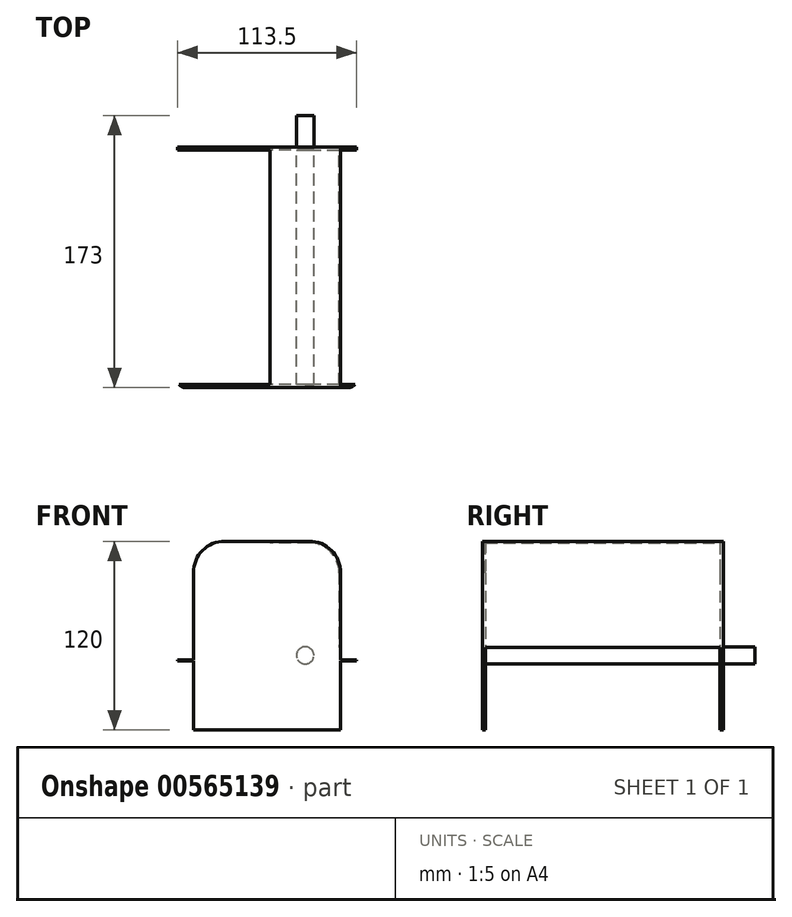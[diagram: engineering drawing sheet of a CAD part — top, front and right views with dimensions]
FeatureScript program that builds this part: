
annotation { "Feature Type Name" : "Feature", "Feature Type Description" : "" }
export const myFeature = defineFeature(function(context is Context, id is Id, definition is map)
    precondition{}
    {
        {
            var Q0;
            Q0=qCreatedBy(makeId("Front.planeOp"),FACE);
            var sketch = newSketch(context, id + "F0", { "sketchPlane" : qUnion([Q0])});
            skLineSegment(sketch, "E0.bottom", {"start": v(46.75, 60) * mm, "end": v(-46.75, 60) * mm});
            skLineSegment(sketch, "E0.top", {"start": v(46.75, -60) * mm, "end": v(-46.75, -60) * mm});
            skLineSegment(sketch, "E0.left", {"start": v(46.75, 60) * mm, "end": v(46.75, -60) * mm});
            skLineSegment(sketch, "E0.right", {"start": v(-46.75, 60) * mm, "end": v(-46.75, -60) * mm});
            skPoint(sketch, "E0.middle", {"position": v(0, 0) * mm});
            skCircle(sketch, "E1", {"center": v(-26.75, 40) * mm, "radius": 20 * mm});
            skPoint(sketch, "E1.first.point", {"position": v(-26.75, 60) * mm});
            skPoint(sketch, "E1.second.point", {"position": v(-46.75, 40) * mm});
            skPoint(sketch, "E1.third.point", {"position": v(-9.2, 30.42) * mm});
            skCircle(sketch, "E2", {"center": v(26.75, 40) * mm, "radius": 20 * mm});
            skPoint(sketch, "E2.first.point", {"position": v(26.75, 60) * mm});
            skPoint(sketch, "E2.second.point", {"position": v(46.75, 40) * mm});
            skPoint(sketch, "E2.third.point", {"position": v(10.34, 28.57) * mm});
            skSolve(sketch);
        }
        {
            var Q0;
            {var subQ1=sQuery(id+"F0.wireOp",EDGE,"E0.top");Q0=makeQuery(id+"F0.imprint","IMPRINT",FACE,{"disambiguationData":[TD([[makeQuery(id+"F0.imprint","IMPRINT",EDGE,{"derivedFrom":subQ1}),-1.0]])]});}
            var Q1;
            {var subQ0=sQuery(id+"F0.wireOp",EDGE,"E2");var subQ1=makeQuery(id+"F0.imprint","INTERSECT",VERTEX,{"derivedFrom":[sQuery(id+"F0.wireOp",EDGE,"E0.bottom"),subQ0]});Q1=makeQuery(id+"F0.imprint","IMPRINT",FACE,{"disambiguationData":[TD([[makeQuery(id+"F0.imprint","IMPRINT",EDGE,{"disambiguationData":[TD([[subQ1,1.0]])],"derivedFrom":subQ0}),1.0]])]});}
            var Q2;
            {var subQ0=sQuery(id+"F0.wireOp",EDGE,"E1");var subQ1=makeQuery(id+"F0.imprint","INTERSECT",VERTEX,{"derivedFrom":[sQuery(id+"F0.wireOp",EDGE,"E0.bottom"),subQ0]});Q2=makeQuery(id+"F0.imprint","IMPRINT",FACE,{"disambiguationData":[TD([[makeQuery(id+"F0.imprint","IMPRINT",EDGE,{"disambiguationData":[TD([[subQ1,-1.0]])],"derivedFrom":subQ0}),1.0]])]});}
            extrude(context, id + "F1", {"entities" : qUnion([Q0, Q1, Q2]), "endBound" : BoundingType.SYMMETRIC, "depth" : 153 * mm, "offsetDistance" : 25 * mm});
        }
        {
            var Q0;
            Q0=makeQuery(id+"F1.opExtrude","CAP_FACE",FACE,{"disambiguationData":[OSD([sQuery(id+"F0.wireOp",EDGE,"E0.bottom"),sQuery(id+"F0.wireOp",EDGE,"E0.top"),sQuery(id+"F0.wireOp",EDGE,"E0.left"),sQuery(id+"F0.wireOp",EDGE,"E0.right"),sQuery(id+"F0.wireOp",EDGE,"E1"),sQuery(id+"F0.wireOp",EDGE,"E2")])],"isStart":false});
            var sketch = newSketch(context, id + "F2", { "sketchPlane" : qUnion([Q0])});
            skLineSegment(sketch, "E3.bottom", {"start": v(56.75, -15.5) * mm, "end": v(-56.75, -15.5) * mm});
            skLineSegment(sketch, "E3.top", {"start": v(56.75, -16) * mm, "end": v(-56.75, -16) * mm});
            skLineSegment(sketch, "E3.left", {"start": v(56.75, -15.5) * mm, "end": v(56.75, -16) * mm});
            skLineSegment(sketch, "E3.right", {"start": v(-56.75, -15.5) * mm, "end": v(-56.75, -16) * mm});
            skSolve(sketch);
        }
        {
            var Q0;
            Q0 = qSketchRegion(id + "F2", true);
            var Q1;
            Q1=makeQuery(id+"F1.opExtrude","CAP_FACE",FACE,{"disambiguationData":[OSD([sQuery(id+"F0.wireOp",EDGE,"E0.bottom"),sQuery(id+"F0.wireOp",EDGE,"E0.top"),sQuery(id+"F0.wireOp",EDGE,"E0.left"),sQuery(id+"F0.wireOp",EDGE,"E0.right"),sQuery(id+"F0.wireOp",EDGE,"E1"),sQuery(id+"F0.wireOp",EDGE,"E2")])],"isStart":true});
            extrude(context, id + "F3", {"entities" : qUnion([Q0]), "operationType" : NewBodyOperationType.ADD, "endBound" : BoundingType.UP_TO_SURFACE, "oppositeDirection" : true, "depth" : 25 * mm, "endBoundEntityFace" : qUnion([Q1]), "offsetDistance" : 25 * mm});
        }
        {
            var Q0;
            Q0=makeQuery(id+"F3.opExtrude","TWEAK_EDGE",EDGE,{"derivedFrom":[makeQuery(id+"F1.opExtrude","CAP_FACE",FACE,{"disambiguationData":[OSD([sQuery(id+"F0.wireOp",EDGE,"E0.bottom"),sQuery(id+"F0.wireOp",EDGE,"E0.top"),sQuery(id+"F0.wireOp",EDGE,"E0.left"),sQuery(id+"F0.wireOp",EDGE,"E0.right"),sQuery(id+"F0.wireOp",EDGE,"E1"),sQuery(id+"F0.wireOp",EDGE,"E2")])],"isStart":true}),makeQuery(id+"F2.imprint","IMPRINT",EDGE,{"derivedFrom":sQuery(id+"F2.wireOp",EDGE,"E3.left")})]});
            var Q1;
            Q1=makeQuery(id+"F3.opExtrude","TWEAK_EDGE",EDGE,{"derivedFrom":[makeQuery(id+"F1.opExtrude","CAP_FACE",FACE,{"disambiguationData":[OSD([sQuery(id+"F0.wireOp",EDGE,"E0.bottom"),sQuery(id+"F0.wireOp",EDGE,"E0.top"),sQuery(id+"F0.wireOp",EDGE,"E0.left"),sQuery(id+"F0.wireOp",EDGE,"E0.right"),sQuery(id+"F0.wireOp",EDGE,"E1"),sQuery(id+"F0.wireOp",EDGE,"E2")])],"isStart":true}),makeQuery(id+"F2.imprint","IMPRINT",EDGE,{"derivedFrom":sQuery(id+"F2.wireOp",EDGE,"E3.right")})]});
            var Q2;
            Q2=makeQuery(id+"F3.opExtrude","CAP_EDGE",EDGE,{"disambiguationData":[OSD([sQuery(id+"F2.wireOp",EDGE,"E3.right")])],"isStart":true});
            var Q3;
            Q3=makeQuery(id+"F3.opExtrude","CAP_EDGE",EDGE,{"disambiguationData":[OSD([sQuery(id+"F2.wireOp",EDGE,"E3.left")])],"isStart":true});
            fillet(context, id + "F4", {"entities" : qUnion([Q0, Q1, Q2, Q3]), "radius" : 5 * mm, "tangentPropagation" : true, "allowEdgeOverflow" : false});
        }
        {
            var Q0;
            {var subQ2=sQuery(id+"F0.wireOp",EDGE,"E0.right");var subQ7=sQuery(id+"F2.wireOp",EDGE,"E3.bottom");Q0=makeQuery(id+"F3.boolean.opBoolean","SPLIT",FACE,{"disambiguationData":[TD([makeQuery(id+"F1.opExtrude","SWEPT_FACE",FACE,{"disambiguationData":[OSD([subQ2])]})])],"derivedFrom":makeQuery(id+"F3.opExtrude","SWEPT_FACE",FACE,{"disambiguationData":[OSD([subQ7])]})});}
            var sketch = newSketch(context, id + "F5", { "sketchPlane" : qUnion([Q0])});
            skLineSegment(sketch, "E4", {"start": v(-56.75, 71.5) * mm, "end": v(-46.75, 71.5) * mm, "construction": true});
            skLineSegment(sketch, "E5", {"start": v(-51.75, 71.5) * mm, "end": v(-51.75, 69.11) * mm, "construction": true});
            skLineSegment(sketch, "E6", {"start": v(-51.75, 62.95) * mm, "end": v(-51.75, 61.45) * mm});
            skArc(sketch, "E7.0.startCap", {"start": v(-53.8, 62.95) * mm, "mid": v(-51.75, 65) * mm, "end": v(-49.7, 62.95) * mm});
            skArc(sketch, "E7.0.endCap", {"start": v(-49.7, 61.45) * mm, "mid": v(-51.75, 59.4) * mm, "end": v(-53.8, 61.45) * mm});
            skLineSegment(sketch, "E7.0.left", {"start": v(-49.7, 62.95) * mm, "end": v(-49.7, 61.45) * mm});
            skLineSegment(sketch, "E7.0.right", {"start": v(-53.8, 62.95) * mm, "end": v(-53.8, 61.45) * mm});
            skLineSegment(sketch, "E8.0.1.0", {"start": v(-51.75, 11.05) * mm, "end": v(-51.75, 9.55) * mm});
            skLineSegment(sketch, "E8.0.1.1", {"start": v(-53.8, 11.05) * mm, "end": v(-53.8, 9.55) * mm});
            skArc(sketch, "E8.0.1.2", {"start": v(-49.7, 9.55) * mm, "mid": v(-51.75, 7.5) * mm, "end": v(-53.8, 9.55) * mm});
            skArc(sketch, "E8.0.1.3", {"start": v(-53.8, 11.05) * mm, "mid": v(-51.75, 13.1) * mm, "end": v(-49.7, 11.05) * mm});
            skLineSegment(sketch, "E8.0.1.4", {"start": v(-49.7, 11.05) * mm, "end": v(-49.7, 9.55) * mm});
            skLineSegment(sketch, "E8.1.0.0", {"start": v(52.25, 62.95) * mm, "end": v(52.25, 61.45) * mm});
            skLineSegment(sketch, "E8.1.0.1", {"start": v(50.2, 62.95) * mm, "end": v(50.2, 61.45) * mm});
            skArc(sketch, "E8.1.0.2", {"start": v(54.3, 61.45) * mm, "mid": v(52.25, 59.4) * mm, "end": v(50.2, 61.45) * mm});
            skArc(sketch, "E8.1.0.3", {"start": v(50.2, 62.95) * mm, "mid": v(52.25, 65) * mm, "end": v(54.3, 62.95) * mm});
            skLineSegment(sketch, "E8.1.0.4", {"start": v(54.3, 62.95) * mm, "end": v(54.3, 61.45) * mm});
            skLineSegment(sketch, "E8.1.1.0", {"start": v(52.25, 11.05) * mm, "end": v(52.25, 9.55) * mm});
            skLineSegment(sketch, "E8.1.1.1", {"start": v(50.2, 11.05) * mm, "end": v(50.2, 9.55) * mm});
            skArc(sketch, "E8.1.1.2", {"start": v(54.3, 9.55) * mm, "mid": v(52.25, 7.5) * mm, "end": v(50.2, 9.55) * mm});
            skArc(sketch, "E8.1.1.3", {"start": v(50.2, 11.05) * mm, "mid": v(52.25, 13.1) * mm, "end": v(54.3, 11.05) * mm});
            skLineSegment(sketch, "E8.1.1.4", {"start": v(54.3, 11.05) * mm, "end": v(54.3, 9.55) * mm});
            skLineSegment(sketch, "E8.direction1", {"start": v(-51.75, 61.45) * mm, "end": v(52.25, 61.45) * mm, "construction": true});
            skLineSegment(sketch, "E8.direction2", {"start": v(-51.75, 61.45) * mm, "end": v(-51.75, 9.55) * mm, "construction": true});
            skLineSegment(sketch, "E9", {"start": v(-56.75, 0) * mm, "end": v(-85.02, 0) * mm, "construction": true});
            skArc(sketch, "E10.MirrorCS", {"start": v(-49.7, -61.45) * mm, "mid": v(-51.75, -59.4) * mm, "end": v(-53.8, -61.45) * mm});
            skArc(sketch, "E11.MirrorCS", {"start": v(-53.8, -11.05) * mm, "mid": v(-51.75, -13.1) * mm, "end": v(-49.7, -11.05) * mm});
            skArc(sketch, "E12.MirrorCS", {"start": v(-49.7, -9.55) * mm, "mid": v(-51.75, -7.5) * mm, "end": v(-53.8, -9.55) * mm});
            skLineSegment(sketch, "E13.MirrorCS", {"start": v(-49.7, -11.05) * mm, "end": v(-49.7, -9.55) * mm});
            skLineSegment(sketch, "E14.MirrorCS", {"start": v(-53.8, -11.05) * mm, "end": v(-53.8, -9.55) * mm});
            skArc(sketch, "E15.MirrorCS", {"start": v(-53.8, -62.95) * mm, "mid": v(-51.75, -65) * mm, "end": v(-49.7, -62.95) * mm});
            skLineSegment(sketch, "E16.MirrorCS", {"start": v(-53.8, -62.95) * mm, "end": v(-53.8, -61.45) * mm});
            skLineSegment(sketch, "E17.MirrorCS", {"start": v(-49.7, -62.95) * mm, "end": v(-49.7, -61.45) * mm});
            skArc(sketch, "E18.MirrorCS", {"start": v(54.3, -9.55) * mm, "mid": v(52.25, -7.5) * mm, "end": v(50.2, -9.55) * mm});
            skArc(sketch, "E19.MirrorCS", {"start": v(50.2, -11.05) * mm, "mid": v(52.25, -13.1) * mm, "end": v(54.3, -11.05) * mm});
            skLineSegment(sketch, "E20.MirrorCS", {"start": v(50.2, -11.05) * mm, "end": v(50.2, -9.55) * mm});
            skLineSegment(sketch, "E21.MirrorCS", {"start": v(54.3, -11.05) * mm, "end": v(54.3, -9.55) * mm});
            skArc(sketch, "E22.MirrorCS", {"start": v(54.3, -61.45) * mm, "mid": v(52.25, -59.4) * mm, "end": v(50.2, -61.45) * mm});
            skArc(sketch, "E23.MirrorCS", {"start": v(50.2, -62.95) * mm, "mid": v(52.25, -65) * mm, "end": v(54.3, -62.95) * mm});
            skLineSegment(sketch, "E24.MirrorCS", {"start": v(50.2, -62.95) * mm, "end": v(50.2, -61.45) * mm});
            skLineSegment(sketch, "E25.MirrorCS", {"start": v(54.3, -62.95) * mm, "end": v(54.3, -61.45) * mm});
            skSolve(sketch);
        }
        {
            var Q0;
            Q0 = qSketchRegion(id + "F5", true);
            extrude(context, id + "F6", {"entities" : qUnion([Q0]), "operationType" : NewBodyOperationType.REMOVE, "endBound" : BoundingType.THROUGH_ALL, "oppositeDirection" : true, "depth" : 25 * mm, "offsetDistance" : 25 * mm});
        }
        {
            var Q0;
            {var subQ0=sQuery(id+"F0.wireOp",EDGE,"E2");var subQ1=sQuery(id+"F0.wireOp",EDGE,"E1");var subQ2=sQuery(id+"F0.wireOp",EDGE,"E0.right");var subQ3=sQuery(id+"F0.wireOp",EDGE,"E0.left");var subQ4=sQuery(id+"F0.wireOp",EDGE,"E0.top");var subQ5=sQuery(id+"F0.wireOp",EDGE,"E0.bottom");Q0=makeQuery(id+"F3.boolean.opBoolean","MERGE",FACE,{"derivedFrom":[makeQuery(id+"F1.opExtrude","CAP_FACE",FACE,{"disambiguationData":[OSD([subQ5,subQ4,subQ3,subQ2,subQ1,subQ0])],"isStart":true}),makeQuery(id+"F3.opExtrude","CAP_FACE",FACE,{"disambiguationData":[OSD([subQ5,subQ4,subQ3,subQ2,subQ1,subQ0])],"isStart":false})]});}
            var sketch = newSketch(context, id + "F7", { "sketchPlane" : qUnion([Q0])});
            skCircle(sketch, "E26", {"center": v(-24.25, -12.5) * mm, "radius": 5.5 * mm});
            skSolve(sketch);
        }
        {
            var Q0;
            Q0 = qSketchRegion(id + "F7", true);
            extrude(context, id + "F8", {"entities" : qUnion([Q0]), "operationType" : NewBodyOperationType.ADD, "depth" : 20 * mm, "offsetDistance" : 25 * mm});
        }
        {
            var Q0;
            Q0=makeQuery(id+"F1.opExtrude","SWEPT_FACE",FACE,{"disambiguationData":[OSD([sQuery(id+"F0.wireOp",EDGE,"E0.top")])]});
            var sketch = newSketch(context, id + "F9", { "sketchPlane" : qUnion([Q0])});
            skLineSegment(sketch, "E27.bottom", {"start": v(-41.25, -56.5) * mm, "end": v(41.25, -56.5) * mm});
            skLineSegment(sketch, "E27.top", {"start": v(-41.25, 56.5) * mm, "end": v(41.25, 56.5) * mm});
            skLineSegment(sketch, "E27.left", {"start": v(-41.25, -56.5) * mm, "end": v(-41.25, 56.5) * mm});
            skLineSegment(sketch, "E27.right", {"start": v(41.25, -56.5) * mm, "end": v(41.25, 56.5) * mm});
            skSolve(sketch);
        }
        {
            var Q0;
            Q0 = qSketchRegion(id + "F9", true);
            extrude(context, id + "F10", {"entities" : qUnion([Q0]), "operationType" : NewBodyOperationType.REMOVE, "oppositeDirection" : true, "depth" : 6 * mm, "offsetDistance" : 25 * mm});
        }
        {
            var Q0;
            {var subQ0=sQuery(id+"F0.wireOp",EDGE,"E2");var subQ1=sQuery(id+"F0.wireOp",EDGE,"E1");var subQ2=sQuery(id+"F0.wireOp",EDGE,"E0.right");var subQ3=sQuery(id+"F0.wireOp",EDGE,"E0.left");var subQ4=sQuery(id+"F0.wireOp",EDGE,"E0.top");var subQ5=sQuery(id+"F0.wireOp",EDGE,"E0.bottom");Q0=makeQuery(id+"F3.boolean.opBoolean","MERGE",FACE,{"derivedFrom":[makeQuery(id+"F1.opExtrude","CAP_FACE",FACE,{"disambiguationData":[OSD([subQ5,subQ4,subQ3,subQ2,subQ1,subQ0])],"isStart":true}),makeQuery(id+"F3.opExtrude","CAP_FACE",FACE,{"disambiguationData":[OSD([subQ5,subQ4,subQ3,subQ2,subQ1,subQ0])],"isStart":false})]});}
            var sketch = newSketch(context, id + "F11", { "sketchPlane" : qUnion([Q0])});
            skLineSegment(sketch, "E28.0", {"start": v(-26.75, 59) * mm, "end": v(26.75, 59) * mm});
            skArc(sketch, "E28.1", {"start": v(-45.75, 40) * mm, "mid": v(-40.19, 53.44) * mm, "end": v(-26.75, 59) * mm});
            skLineSegment(sketch, "E28.2", {"start": v(-45.75, 40) * mm, "end": v(-45.75, -15.5) * mm});
            skLineSegment(sketch, "E29.0", {"start": v(-26.75, 54) * mm, "end": v(26.75, 54) * mm});
            skArc(sketch, "E29.1", {"start": v(-40.75, 40) * mm, "mid": v(-36.65, 49.9) * mm, "end": v(-26.75, 54) * mm});
            skLineSegment(sketch, "E29.2", {"start": v(-40.75, 40) * mm, "end": v(-40.75, -15.5) * mm});
            skArc(sketch, "E30.0", {"start": v(-46.75, 40) * mm, "mid": v(-40.9, 54.14) * mm, "end": v(-26.75, 60) * mm});
            skLineSegment(sketch, "E31.0", {"start": v(-26.75, 60) * mm, "end": v(26.75, 60) * mm});
            skLineSegment(sketch, "E32.0", {"start": v(-46.75, 40) * mm, "end": v(-46.75, -15.5) * mm});
            skLineSegment(sketch, "E33", {"start": v(-46.75, -7.5) * mm, "end": v(-45.75, -7.5) * mm});
            skLineSegment(sketch, "E34", {"start": v(0, 60) * mm, "end": v(0, 49.87) * mm, "construction": true});
            skLineSegment(sketch, "E35", {"start": v(-2, 60) * mm, "end": v(-2, 59) * mm});
            skSolve(sketch);
        }
        {
            var Q0;
            {var subQ2=sQuery(id+"F11.wireOp",EDGE,"E28.1");Q0=makeQuery(id+"F11.imprint","IMPRINT",FACE,{"disambiguationData":[TD([[makeQuery(id+"F11.imprint","IMPRINT",EDGE,{"derivedFrom":subQ2}),1.0]])]});}
            var Q1;
            Q1=makeQuery(id+"F3.boolean.opBoolean","MERGE",FACE,{"derivedFrom":[makeQuery(id+"F1.opExtrude","CAP_FACE",FACE,{"disambiguationData":[OSD([sQuery(id+"F0.wireOp",EDGE,"E0.bottom"),sQuery(id+"F0.wireOp",EDGE,"E0.top"),sQuery(id+"F0.wireOp",EDGE,"E0.left"),sQuery(id+"F0.wireOp",EDGE,"E0.right"),sQuery(id+"F0.wireOp",EDGE,"E1"),sQuery(id+"F0.wireOp",EDGE,"E2")])],"isStart":false}),makeQuery(id+"F3.opExtrude","CAP_FACE",FACE,{"disambiguationData":[OSD([sQuery(id+"F2.wireOp",EDGE,"E3.bottom"),sQuery(id+"F2.wireOp",EDGE,"E3.top"),sQuery(id+"F2.wireOp",EDGE,"E3.left"),sQuery(id+"F2.wireOp",EDGE,"E3.right")])],"isStart":true})]});
            extrude(context, id + "F12", {"entities" : qUnion([Q0]), "operationType" : NewBodyOperationType.REMOVE, "endBound" : BoundingType.UP_TO_SURFACE, "oppositeDirection" : true, "depth" : 2 * mm, "endBoundEntityFace" : qUnion([Q1]), "hasOffset" : true, "offsetDistance" : 2 * mm, "hasSecondDirection" : true, "secondDirectionOppositeDirection" : true, "secondDirectionDepth" : 2 * mm, "hasSecondDirectionOffset" : true, "secondDirectionOffsetDistance" : 25 * mm, "secondDirectionOffsetOppositeDirection" : true});
        }
    });
